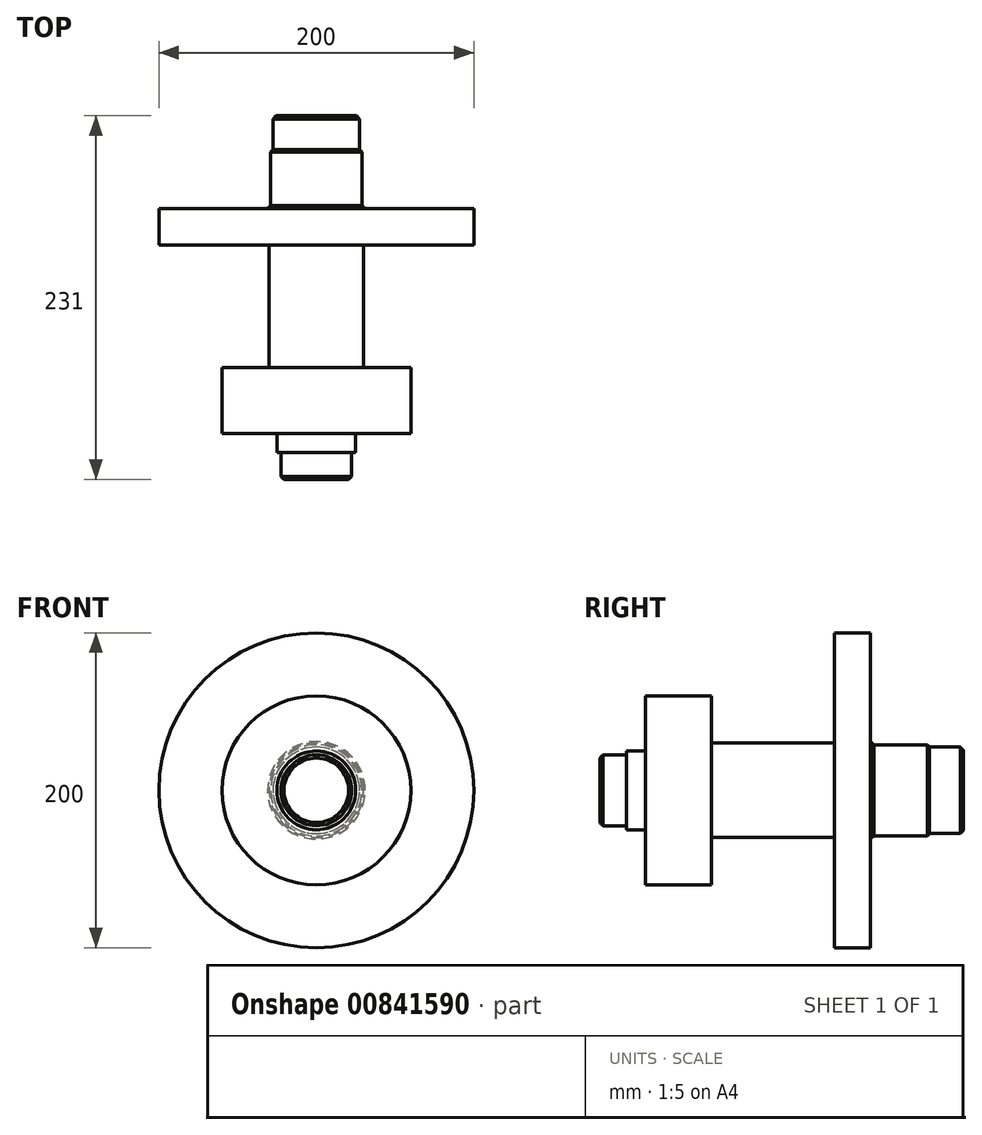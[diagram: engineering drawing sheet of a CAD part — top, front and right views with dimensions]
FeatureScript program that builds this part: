
annotation { "Feature Type Name" : "Feature", "Feature Type Description" : "" }
export const myFeature = defineFeature(function(context is Context, id is Id, definition is map)
    precondition{}
    {
        {
            var Q0;
            Q0=qCreatedBy(makeId("Top.planeOp"),FACE);
            var sketch = newSketch(context, id + "F0", { "sketchPlane" : qUnion([Q0])});
            skLineSegment(sketch, "E0", {"start": v(0, 0) * mm, "end": v(0, 231) * mm});
            skLineSegment(sketch, "E1", {"start": v(0, 231) * mm, "end": v(-27.5, 231) * mm});
            skLineSegment(sketch, "E2", {"start": v(-29, 210) * mm, "end": v(-29, 172) * mm});
            skLineSegment(sketch, "E3", {"start": v(-29, 172) * mm, "end": v(-100, 172) * mm});
            skLineSegment(sketch, "E4", {"start": v(-100, 172) * mm, "end": v(-100, 149) * mm});
            skLineSegment(sketch, "E5", {"start": v(-30, 149) * mm, "end": v(-100, 149) * mm});
            skLineSegment(sketch, "E6", {"start": v(-30, 149) * mm, "end": v(-30, 71) * mm});
            skLineSegment(sketch, "E7", {"start": v(-30, 71) * mm, "end": v(-60, 71) * mm});
            skLineSegment(sketch, "E8", {"start": v(-60, 71) * mm, "end": v(-60, 29) * mm});
            skLineSegment(sketch, "E9", {"start": v(-60, 29) * mm, "end": v(-25, 29) * mm});
            skLineSegment(sketch, "E10", {"start": v(-25, 29) * mm, "end": v(-25, 17) * mm});
            skLineSegment(sketch, "E11", {"start": v(-25, 17) * mm, "end": v(-22.5, 17) * mm});
            skLineSegment(sketch, "E12", {"start": v(-22.5, 17) * mm, "end": v(-22.5, 0) * mm});
            skLineSegment(sketch, "E13", {"start": v(-22.5, 0) * mm, "end": v(0, 0) * mm});
            skLineSegment(sketch, "E14", {"start": v(0, 231) * mm, "end": v(0, -11.58) * mm, "construction": true});
            skLineSegment(sketch, "E15", {"start": v(-29, 210) * mm, "end": v(-27.5, 210) * mm});
            skLineSegment(sketch, "E16", {"start": v(-27.5, 210) * mm, "end": v(-27.5, 231) * mm});
            skSolve(sketch);
        }
        {
            var Q0;
            Q0=makeQuery(id+"F0.imprint","IMPRINT",FACE,{"disambiguationData":[TD([[makeQuery(id+"F0.imprint","IMPRINT",EDGE,{"derivedFrom":sQuery(id+"F0.wireOp",EDGE,"E0")}),1.0]])]});
            var Q1;
            Q1=sQuery(id+"F0.wireOp",EDGE,"E14");
            revolve(context, id + "F1", {"surfaceOperationType" : NewSurfaceOperationType.NEW, "entities" : qUnion([Q0]), "axis" : qUnion([Q1]), "revolveType" : RevolveType.FULL});
        }
        {
            var Q0;
            Q0=makeQuery(id+"F1.opRevolve","SWEPT_EDGE",EDGE,{"disambiguationData":[OSD([sQuery(id+"F0.wireOp",EDGE,"E1"),sQuery(id+"F0.wireOp",EDGE,"E2")])]});
            var Q1;
            Q1=makeQuery(id+"F1.opRevolve","SWEPT_EDGE",EDGE,{"disambiguationData":[OSD([sQuery(id+"F0.wireOp",EDGE,"E12"),sQuery(id+"F0.wireOp",EDGE,"E13")])]});
            chamfer(context, id + "F2", {"entities" : qUnion([Q0, Q1]), "width" : 2 * mm, "tangentPropagation" : true});
        }
    });
